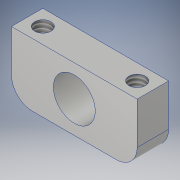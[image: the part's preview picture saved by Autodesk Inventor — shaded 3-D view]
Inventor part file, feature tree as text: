
AUTODESK INVENTOR PART (.ipt)
format: ipt  version: 2017 (Build 210142000, 142)  size: 139,776 bytes
history: native  units: in
note: dims shown in document units (in); Inventor stores cm internally (conversion verified against a paired STEP export)
features: sketch x2, extrude x1, fillet x1, hole x1, mirror x1, projected_geometry x1
ambient origin geometry x8: Origin, YZ Plane, XZ Plane, XY Plane, X Axis, Y Axis, Z Axis, Center Point
bodies: Solid1 (feature_tree)
feature tree (7):
  extrude  "Extrusion1"  Depth=0.75in
  fillet  "Fillet1"  Radius=0.75in
  hole  "Hole1"  [1 undecoded]
  mirror  "Mirror1"
  sketch  "Sketch1"  dims[d0=0.5in d1=0.75in d2=0.75in]
  sketch  "Sketch2"  dims[d3=0.75in d4=0.375in d5=0.0in d6=0.25in d7=0.1875in d9=0.375in d10=0.196in d11=0.4375in d12=0.375in d13=0.25in d14=0.5635in d15=0.4375in d16=0.8108in d17=0.3125in]
  projected_geometry  "Projected Loop1"
note: 1 required parameter value undecoded (feature->parameter linkage not recoverable at this tier; creation-order binding heuristic only, values carry confidence <= 0.55)
